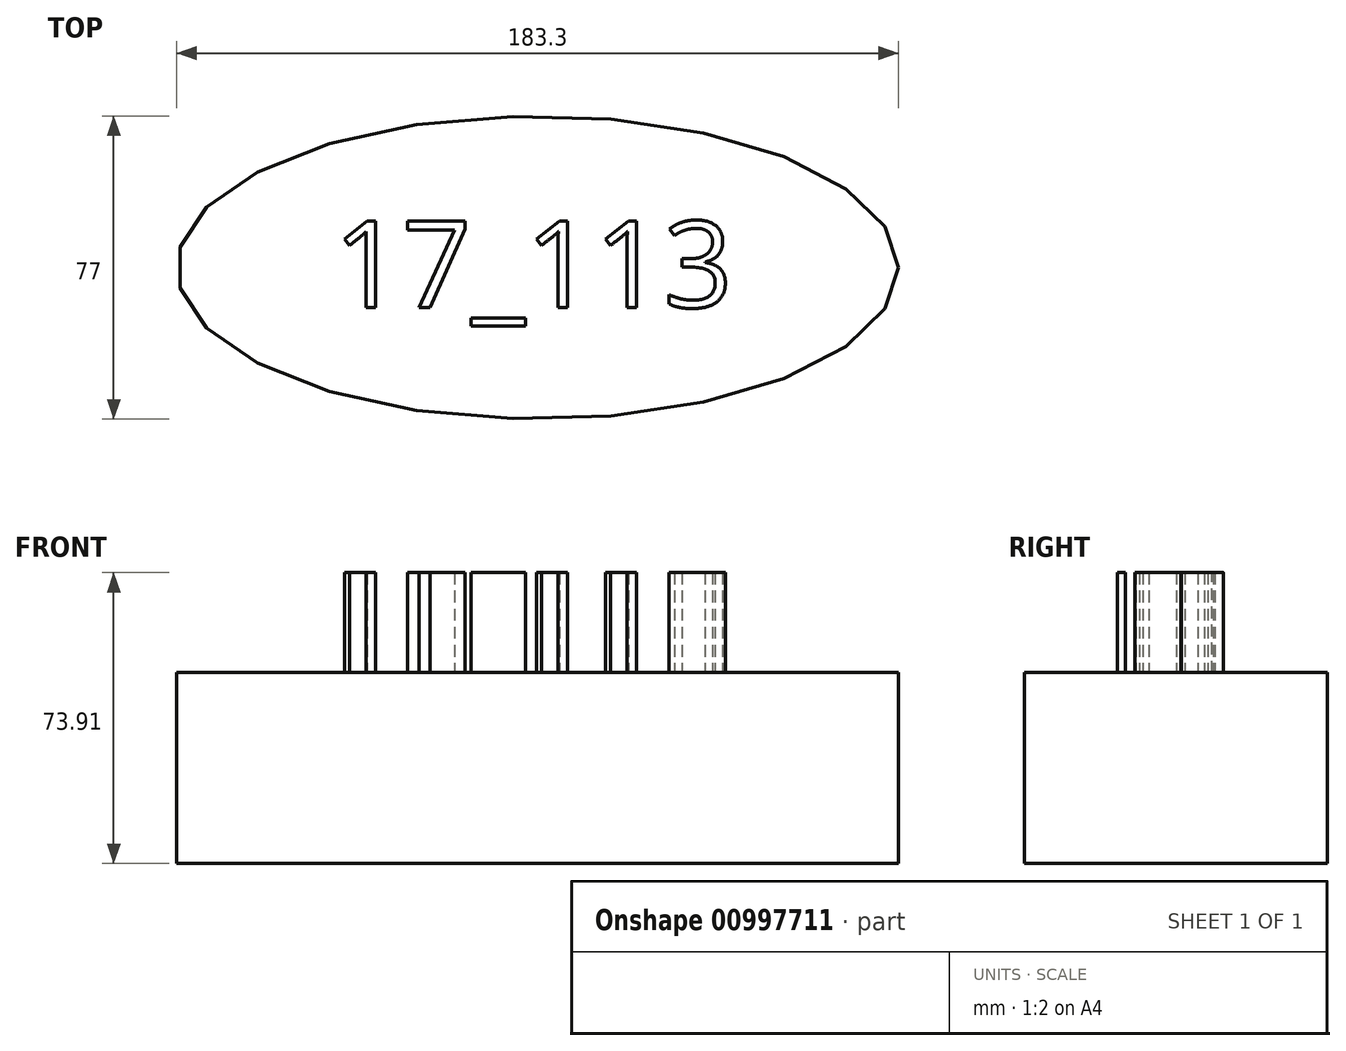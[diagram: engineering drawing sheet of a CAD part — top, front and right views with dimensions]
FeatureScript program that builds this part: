
annotation { "Feature Type Name" : "Feature", "Feature Type Description" : "" }
export const myFeature = defineFeature(function(context is Context, id is Id, definition is map)
    precondition{}
    {
        {
            var Q0;
            Q0=qCreatedBy(makeId("Top.planeOp"),FACE);
            var sketch = newSketch(context, id + "F0", { "sketchPlane" : qUnion([Q0])});
            skEllipse(sketch, "E0", {"center": v(0, 0) * mm, "majorRadius": 91.65 * mm, "minorRadius": 38.5 * mm, "majorAxis": v(1, 0)});
            skSolve(sketch);
        }
        {
            var Q0;
            Q0=makeQuery(id+"F0.imprint","IMPRINT",FACE,{"disambiguationData":[TD([[makeQuery(id+"F0.imprint","IMPRINT",EDGE,{"derivedFrom":sQuery(id+"F0.wireOp",EDGE,"E0")}),1.0]])]});
            extrude(context, id + "F1", {"entities" : qUnion([Q0]), "depth" : 48.5 * mm, "offsetDistance" : 25.4 * mm});
        }
        {
            var Q0;
            Q0=makeQuery(id+"F1.opExtrude","CAP_FACE",FACE,{"disambiguationData":[OSD([sQuery(id+"F0.wireOp",EDGE,"E0")])],"isStart":false});
            var sketch = newSketch(context, id + "F2", { "sketchPlane" : qUnion([Q0])});
            skText(sketch, "E1", { "text": "17_113", "fontName": "OpenSans-Regular.ttf"});
            const initialGuessF2  = {"E1": [-0.05191, -0.01012, 1, 0, 0.02208]};
            skSetInitialGuess(sketch, initialGuessF2);
            skSolve(sketch);
        }
        {
            var Q0;
            Q0 = qSketchRegion(id + "F2", true);
            extrude(context, id + "F3", {"entities" : qUnion([Q0]), "operationType" : NewBodyOperationType.ADD, "depth" : 25.4 * mm, "offsetDistance" : 25.4 * mm});
        }
    });
